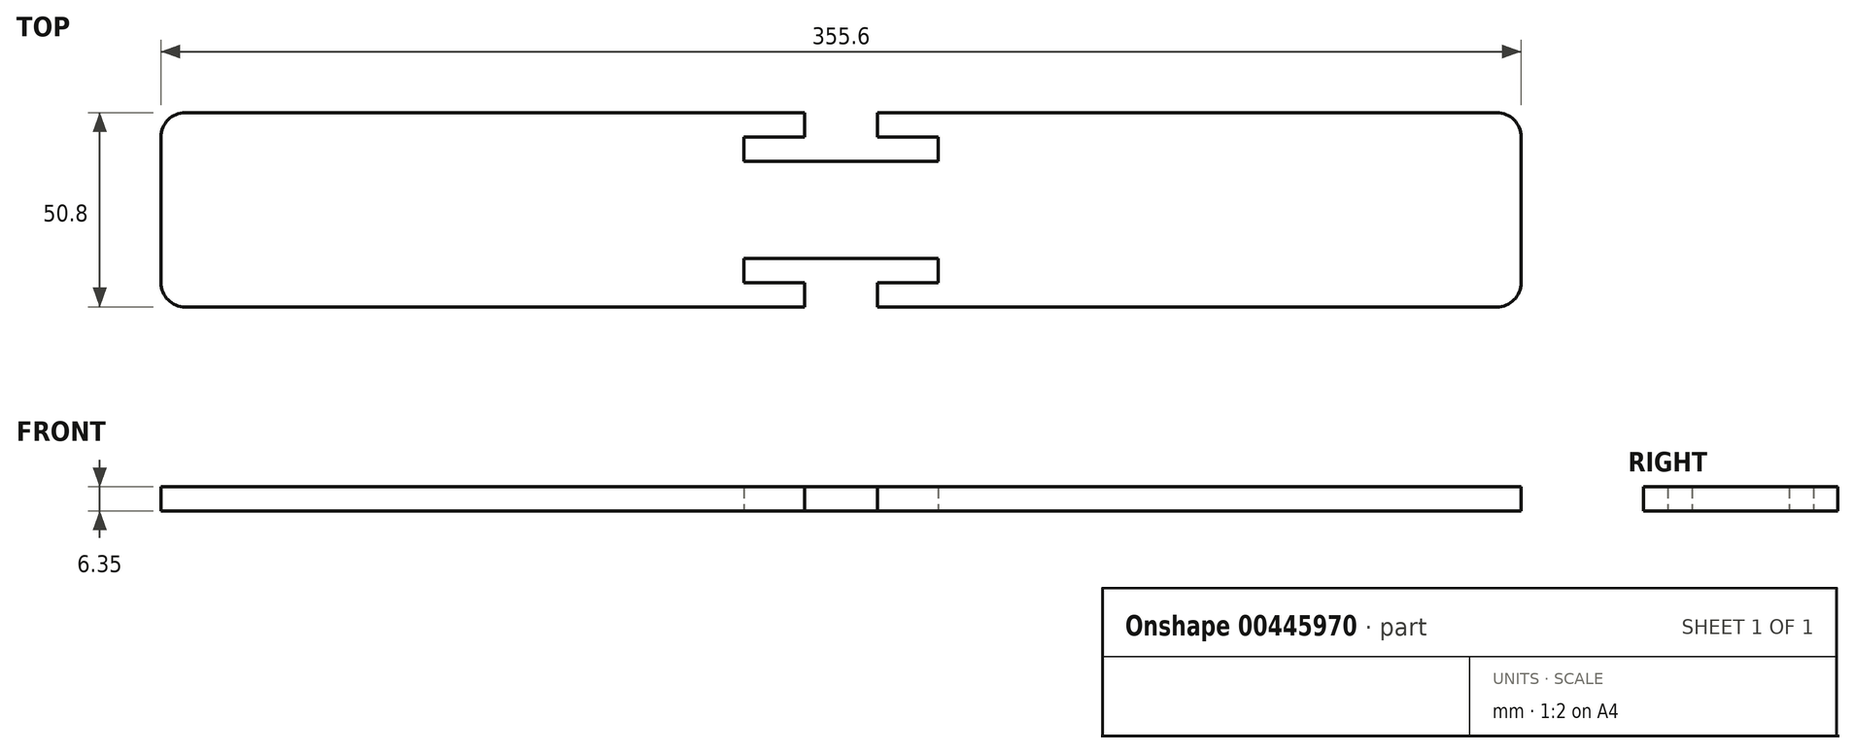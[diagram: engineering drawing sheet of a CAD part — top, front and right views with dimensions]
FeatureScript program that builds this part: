
annotation { "Feature Type Name" : "Feature", "Feature Type Description" : "" }
export const myFeature = defineFeature(function(context is Context, id is Id, definition is map)
    precondition{}
    {
        {
            var Q0;
            Q0=qCreatedBy(makeId("Top.planeOp"),FACE);
            var sketch = newSketch(context, id + "F0", { "sketchPlane" : qUnion([Q0])});
            skLineSegment(sketch, "E0.bottom", {"start": v(-130.77, 12.7) * mm, "end": v(212.13, 12.7) * mm});
            skLineSegment(sketch, "E0.top", {"start": v(-130.77, -38.1) * mm, "end": v(212.13, -38.1) * mm});
            skLineSegment(sketch, "E0.left", {"start": v(-137.12, 6.35) * mm, "end": v(-137.12, -31.75) * mm});
            skLineSegment(sketch, "E0.right", {"start": v(218.48, 6.35) * mm, "end": v(218.48, -31.75) * mm});
            skLineSegment(sketch, "E1.bottom", {"start": v(15.28, 6.35) * mm, "end": v(66.08, 6.35) * mm});
            skLineSegment(sketch, "E1.top", {"start": v(15.28, 0) * mm, "end": v(66.08, 0) * mm});
            skLineSegment(sketch, "E1.left", {"start": v(15.28, 6.35) * mm, "end": v(15.28, 0) * mm});
            skLineSegment(sketch, "E1.right", {"start": v(66.08, 6.35) * mm, "end": v(66.08, 0) * mm});
            skLineSegment(sketch, "E2", {"start": v(15.28, 6.35) * mm, "end": v(15.28, 12.7) * mm});
            skLineSegment(sketch, "E3", {"start": v(66.08, 6.35) * mm, "end": v(66.08, 12.7) * mm});
            skLineSegment(sketch, "E4.bottom", {"start": v(15.28, -25.4) * mm, "end": v(66.08, -25.4) * mm});
            skLineSegment(sketch, "E4.top", {"start": v(15.28, -31.75) * mm, "end": v(66.08, -31.75) * mm});
            skLineSegment(sketch, "E4.left", {"start": v(15.28, -25.4) * mm, "end": v(15.28, -31.75) * mm});
            skLineSegment(sketch, "E4.right", {"start": v(66.08, -25.4) * mm, "end": v(66.08, -31.75) * mm});
            skLineSegment(sketch, "E5", {"start": v(15.28, -31.75) * mm, "end": v(15.28, -38.1) * mm});
            skLineSegment(sketch, "E6", {"start": v(66.08, -31.75) * mm, "end": v(66.08, -38.1) * mm});
            skLineSegment(sketch, "E7", {"start": v(31.15, 6.35) * mm, "end": v(31.15, 12.7) * mm});
            skLineSegment(sketch, "E8", {"start": v(50.2, 6.35) * mm, "end": v(50.2, 12.7) * mm});
            skPoint(sketch, "E8.endSnap0", {"position": v(40.68, 12.7) * mm});
            skLineSegment(sketch, "E9", {"start": v(31.15, -31.75) * mm, "end": v(31.15, -38.1) * mm});
            skLineSegment(sketch, "E10", {"start": v(50.2, -31.75) * mm, "end": v(50.2, -38.1) * mm});
            skPoint(sketch, "E11.visualSharp", {"position": v(218.48, 12.7) * mm});
            skArc(sketch, "E11.filletArc", {"start": v(218.48, 6.35) * mm, "mid": v(216.62, 10.84) * mm, "end": v(212.13, 12.7) * mm});
            skPoint(sketch, "E12.visualSharp", {"position": v(218.48, -38.1) * mm});
            skArc(sketch, "E12.filletArc", {"start": v(212.13, -38.1) * mm, "mid": v(216.62, -36.24) * mm, "end": v(218.48, -31.75) * mm});
            skPoint(sketch, "E13.visualSharp", {"position": v(-137.12, -38.1) * mm});
            skArc(sketch, "E13.filletArc", {"start": v(-137.12, -31.75) * mm, "mid": v(-135.26, -36.24) * mm, "end": v(-130.77, -38.1) * mm});
            skPoint(sketch, "E14.visualSharp", {"position": v(-137.12, 12.7) * mm});
            skArc(sketch, "E14.filletArc", {"start": v(-130.77, 12.7) * mm, "mid": v(-135.26, 10.84) * mm, "end": v(-137.12, 6.35) * mm});
            skSolve(sketch);
        }
        {
            var Q0;
            {var subQ1=sQuery(id+"F0.wireOp",EDGE,"E0.left");Q0=makeQuery(id+"F0.imprint","IMPRINT",FACE,{"disambiguationData":[TD([[makeQuery(id+"F0.imprint","IMPRINT",EDGE,{"derivedFrom":subQ1}),1.0]])]});}
            var Q1;
            {var subQ0=sQuery(id+"F0.wireOp",EDGE,"E2");Q1=makeQuery(id+"F0.imprint","IMPRINT",FACE,{"disambiguationData":[TD([[makeQuery(id+"F0.imprint","IMPRINT",EDGE,{"derivedFrom":subQ0}),-1.0]])]});}
            var Q2;
            {var subQ0=sQuery(id+"F0.wireOp",EDGE,"E3");Q2=makeQuery(id+"F0.imprint","IMPRINT",FACE,{"disambiguationData":[TD([[makeQuery(id+"F0.imprint","IMPRINT",EDGE,{"derivedFrom":subQ0}),1.0]])]});}
            var Q3;
            {var subQ0=sQuery(id+"F0.wireOp",EDGE,"E6");Q3=makeQuery(id+"F0.imprint","IMPRINT",FACE,{"disambiguationData":[TD([[makeQuery(id+"F0.imprint","IMPRINT",EDGE,{"derivedFrom":subQ0}),-1.0]])]});}
            var Q4;
            {var subQ0=sQuery(id+"F0.wireOp",EDGE,"E5");Q4=makeQuery(id+"F0.imprint","IMPRINT",FACE,{"disambiguationData":[TD([[makeQuery(id+"F0.imprint","IMPRINT",EDGE,{"derivedFrom":subQ0}),1.0]])]});}
            extrude(context, id + "F1", {"entities" : qUnion([Q0, Q1, Q2, Q3, Q4]), "depth" : 6.35 * mm, "offsetDistance" : 25.4 * mm});
        }
    });
